# Revit family: MXP-Aisle-Hussey-Portable-Quattro-Nose_Mount
name_source: partatom
category: Specialty Equipment
units: mm (PartAtom-declared; Revit-internal decimal feet)

## family parameters
Always vertical = Yes
Cut with Voids When Loaded = No
Enable Cutting in Views = No
Maintain Annotation Orientation = No
OmniClass Number = 23.40.50.34.14
OmniClass Title = Gymnasium Equipment
Part Type = Normal
Room Calculation Point = No
Round Connector Dimension = Use Diameter
Shared = No
Work Plane-Based = No

## types (5) — shared parameters
Aisle Step Material = Hussey - Polymer - 050 Grey
Assembly Code = E1020900
BIM Version = v3.1
BIM Version Available (Earliest) = 2017
CSI MasterFormat = 12 66 00
Deck Material = Hussey - Decking - AlumaDeck - 005 Aluminum
Default Elevation = 0"
Description = MXP Telescopic Platform Aisle with Nose Mount Quattro Chairs and Tapered End Option - Portable
End Rail Color = Hussey - Powder Coat - 050 Grey
Front Closure Material = Hussey - Powder Coat - 983 Black
MXP Literature Downloads = http://www.husseyseating.com
Manufacturer = Hussey Seating Company
Model = MXP
Nose Beam Material = Hussey - Galvanized Steel
Not Quattro Chair = No
Product Page URL = http://www.husseyseating.com
Quattro Chair = Yes
Quattro Product Selector Worksheet = http://www.husseyseating.com
Riser Material = Hussey - Powder Coat - 983 Black
Row Spacing Note = 32'', 33'', 34'', 35'' or 36''
Type Comments = Telescopic Platform Aisle
URL = http://www.husseyseating.com

## per-type parameters (varying)
| type | Row Spacing |
| 32" Row Spacing | 2' - 8" |
| 33" Row Spacing | 2' - 9" |
| 34" Row Spacing | 2' - 10" |
| 35" Row Spacing | 2' - 11" |
| 36" Row Spacing | 3' - 0" |

## geometry (parser evidence)
native form markers: Blend x39, Extrusion x4, Sweep x23
no freeform markers — native parametric forms only
